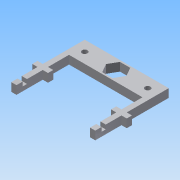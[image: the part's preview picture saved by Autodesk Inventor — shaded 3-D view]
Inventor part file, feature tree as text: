
AUTODESK INVENTOR PART (.ipt)
format: ipt  version: 2015 (Build 190159000, 159)  size: 187,392 bytes
history: native  units: mm
features: extrude x5, sketch x4, projected_geometry x4, reference x2
ambient origin geometry x8: Origin, YZ Plane, XZ Plane, XY Plane, X Axis, Y Axis, Z Axis, Center Point
bodies: Solid1 (feature_tree)
feature tree (15):
  extrude  "Extrusion1"  Depth=20.0mm
  extrude  "Extrusion2"  Depth=10.0mm TaperAngle=0.0deg
  extrude  "Extrusion3"  Depth=60.0mm
  extrude  "Extrusion8"  Depth=8.0mm
  extrude  "Extrusion9"  Depth=40.0mm
  sketch  "Sketch3"  dims[d0=80.0mm d1=20.0mm]
  sketch  "Sketch9"  dims[d2=8.0mm d3=0.0mm d13=10.0mm d14=0.0mm]
  reference  "Reference1"
  reference  "Reference2"
  sketch  "Sketch14"  dims[d40=5.2mm d41=60.0mm]
  projected_geometry  "Projected Loop2"
  sketch  "Sketch15"  dims[d42=10.0mm d43=0.0mm d65=19.5mm d70=40.0mm d73=10.0mm d74=5.0mm d75=50.0mm d78=5.0mm d79=5.0mm d80=5.0mm d81=20.0mm d82=8.0mm d83=0.0mm d84=4.0mm d85=4.0mm d86=6.0mm d87=8.0mm d88=0.0mm]
  projected_geometry  "Projected Loop3"
  projected_geometry  "Projected Loop4"
  projected_geometry  "Projected Loop5"
